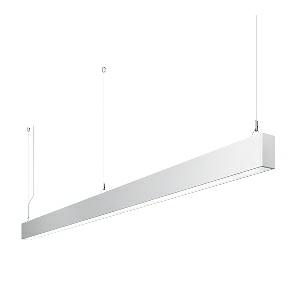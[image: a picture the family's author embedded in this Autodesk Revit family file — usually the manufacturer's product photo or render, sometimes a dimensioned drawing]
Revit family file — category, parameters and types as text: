
# Revit family: dotoo_line_-_dlp_3000_840_d_00805784_2419
name_source: partatom
category: Lighting Fixtures
units: mm (PartAtom-declared; Revit-internal decimal feet)

## family parameters
Cut with Voids When Loaded = No
Host = Face
Light Source = No
Part Type = Normal
Room Calculation Point = No
Round Connector Dimension = Use Diameter
Shared = No

## types (1)
- DOTOO.line - DLP 3000/840/D (1 x LED, 2750 lm, 4000K)
    Apparent Load = 26 VA
    Approval mark = CE
    CIE Flux Codes = 67 91 98 100 100
    Color Rendering = 80-89
    Color Temperature = 4000K
    Control Gear = Electronic ballast
    Default Elevation = 1800 mm
    Description = DLP 3000/840/D|Suspended luminaire|light source: LED|connected load: 220-240 V, 50/60 Hz|Power consumption: approx. 26 W|standby: approx. 0,15|luminous flux: 2750 lm|luminous efficacy: 105 lm/W|light distribution: Direct|direct ratio: approx. 100 %|colour temperature: Cold white, ca. 4000 K|color rendering index (CRI): >= 80|chromaticity tolerance:  3 SDCM|System of protection: IP 40|technology: Continuously dimmable|luminaire body|material: Sectional aluminium|colour: White|lamp cover: Acrylic (PMMA), Clear|mains lead: 2.00 m With free stranded wires|Fastening: Steel cable 0.3 - 0.7 m|glare control: Prism aperture|luminance(L65): <= 3000 cd/m|unified glare rating(4H 8H): <=  19|special features: DALI Load 1x, TouchDIM - dimming via standard switch, Flicker-free, Suitable as emergency lighting|
    Frequency = 50 Hz
    Height = 110 mm
    Lamp = 1 x LED
    Lamp Light Flux = 2750 lm
    Lamp count = 1
    Length = 2256 mm
    Luminous efficacy = 106 lm/W
    Manufacturer = Waldmann
    ModVariant = No
    Model = 00805784
    Mounting Place = Ceiling
    Mounting Type = Pendant
    Number of Poles = 1
    OnlyDefault = Yes
    Power Factor = 1
    Product Name = DOTOO.line - DLP 3000/840/D
    Product group = Suspended luminaire
    ProductGroupID = 9
    Protection Class = Protection class I
    Protection Degree = IP 40
    RLX_Detail_Level = 1
    RLX_Emergency_Light_Flux = 0 lm
    RLX_Emergency_Type = 0
    RLX_Emergency_Type_DB = No
    RlxData = <blob elided: 21373 chars, md5=e703d154>
    Socket = socket
    Standby Power = 0 W
    System Light Flux = 2750 lm
    System Power = 26 W
    Type Comments = Product without accessories
    Type Image = 113293000-00692530.jpg
    URL = http://relux.com
    VarID = ---
    Voltage = 230 V
    Voltage Range = 220-240 V
    Weight = 0.00 kg
    Width = 60 mm

## geometry (parser evidence)
native form markers: Blend x4, Sweep x10
no freeform markers — native parametric forms only
